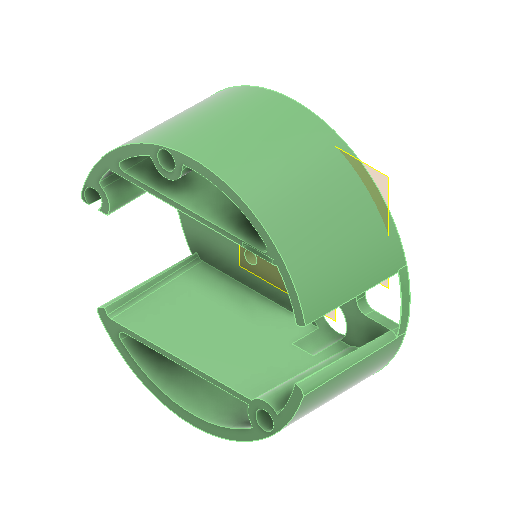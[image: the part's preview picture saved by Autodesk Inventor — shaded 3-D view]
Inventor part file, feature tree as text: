
AUTODESK INVENTOR PART (.ipt)
format: ipt  version: 2022 (Build 260153000, 153)  size: 680,960 bytes
history: native  units: in
note: dims shown in document units (in); Inventor stores cm internally (conversion verified against a paired STEP export)
features: extrude x14, sketch x14, other x9, reference x7, plane x5, projected_geometry x2, fillet x1
ambient origin geometry x8: Origin, YZ Plane, XZ Plane, XY Plane, X Axis, Y Axis, Z Axis, Center Point
bodies: Solid1 (feature_tree)
feature tree (52):
  plane  "Arbeitsebene6"
  extrude  "Extrusion1"  Depth=0.315in
  extrude  "Extrusion2"  Depth=1.0in
  plane  "Arbeitsebene3"
  extrude  "Extrusion6"  Depth=0.1102in
  plane  "Arbeitsebene2"
  extrude  "Extrusion7"  Depth=0.0787in
  extrude  "Extrusion10"  Depth=0.0394in TaperAngle=0.0deg
  plane  "Arbeitsebene7"
  sketch  "Skizze16"  dims[d81=0.0591in d82=0.3937in d83=0.0069in]
  plane  "Arbeitsebene5"
  extrude  "Extrusion14"  Depth=0.3937in
  extrude  "Extrusion15"  Depth=0.3937in
  extrude  "Extrusion17"  TaperAngle=0.0deg  [1 undecoded]
  extrude  "Extrusion18"  Depth=0.1575in
  extrude  "Extrusion19"  Depth=0.1575in
  extrude  "Extrusion20"  Depth=0.8465in TaperAngle=0.0deg
  fillet  "Rundung2"  Radius=0.1614in
  extrude  "Extrusion21"  Depth=0.1614in
  extrude  "Extrusion22"  Depth=0.315in
  extrude  "Extrusion23"  Depth=0.0591in
  sketch  "Sketch1"  dims[d0=0.0787in d1=-0.0069in d2=0.315in]
  sketch  "Sketch2"  dims[d3=0.3189in d4=1.0in d5=-0.0137in]
  sketch  "Sketch8"  dims[d33=0.1102in d34=0.1102in]
  sketch  "Sketch9"  dims[d35=0.0in d36=0.0in d37=0.0787in]
  sketch  "Skizze12"  dims[d38=0.0004in d39=-0.0069in d51=0.0394in d52=0.0in]
  sketch  "Skizze17"  dims[d89=0.3937in d90=-0.0069in d91=0.0787in]
  reference  "Referenz44"
  reference  "Referenz45"
  projected_geometry  "Projizierte Kontur4"
  sketch  "Skizze19"  dims[d92=0.0787in d93=0.0in]
  sketch  "Skizze20"  dims[d94=0.0in d104=0.1575in]
  sketch  "Skizze21"  dims[d105=0.1575in d106=0.1575in]
  sketch  "Skizze22"  dims[d107=0.0001in d108=-0.0069in d109=0.8465in d110=0.0in d111=0.1614in]
  reference  "Referenz46"
  sketch  "Skizze23"  dims[d112=0.1614in d113=0.1614in]
  sketch  "Skizze24"  dims[d114=0.1969in d115=-0.0069in d116=0.315in]
  projected_geometry  "Projizierte Kontur5"
  reference  "Referenz47"
  sketch  "Skizze25"  dims[d117=0.315in d118=0.0069in d119=0.0394in d120=0.0394in d122=0.9055in d123=0.4528in d124=1.8701in d125=0.2756in d126=0.4724in d127=0.5906in d128=0.0394in d129=0.0in d130=0.315in d131=0.315in d132=0.1102in d133=0.1102in d134=0.0in d135=0.0in d136=1.4961in d137=0.315in d138=0.315in d139=0.0591in d140=0.0in d78=0.0197in d79=0.0344in d80=0.0197in d95=0.0197in d96=0.0344in d97=0.0197in d98=0.0344in]
  reference  "Referenz48"
  reference  "Referenz49"
  reference  "Referenz50"
  other  "Matchboxscope_VCM_v1.iam"
  other  "Matchboxscope_bottom_v0:2"
  other  "Matchboxscope_middle2_m12VCMLens_v2:2"
  other  "Spectroscope_v0.iam"
  other  "IM_Matchboxscope_plate:1"
  other  "Assembly_Matchboxscope_injectionmolded_ESPectrometer.iam"
  other  "IM_Matchboxscope_plate:2"
  other  "IM_Lensholder:1"
  other  "DIN 912 - ersetzt durch DIN EN ISO 4762 M3 x 10:3"
note: 1 required parameter value undecoded (feature->parameter linkage not recoverable at this tier; creation-order binding heuristic only, values carry confidence <= 0.55)
